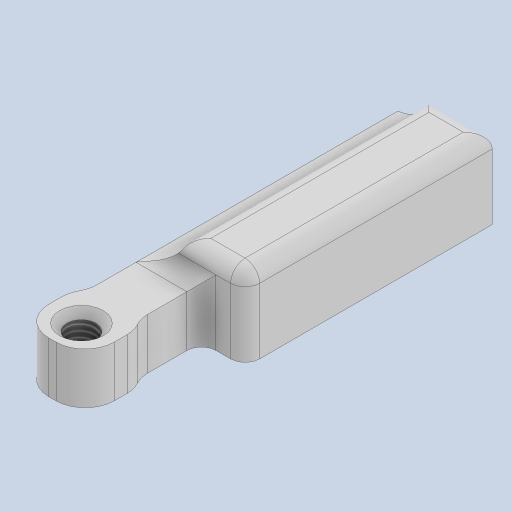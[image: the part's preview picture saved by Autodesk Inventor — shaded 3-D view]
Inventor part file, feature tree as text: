
AUTODESK INVENTOR PART (.ipt)
format: ipt  version: 2023 (Build 270158000, 158)  size: 300,544 bytes
history: native  units: mm
features: extrude x11, sketch x11, fillet x8, other x3, thread x3, chamfer x2
ambient origin geometry x8: Origin, YZ Plane, XZ Plane, XY Plane, X Axis, Y Axis, Z Axis, Center Point
bodies: Body1 (feature_tree)
feature tree (38):
  other  "Твердое тело1"
  extrude  "Выдавливание1"  Depth=3.5mm
  extrude  "Выдавливание2"  Depth=70.0mm
  extrude  "Выдавливание3"  Depth=3.5mm TaperAngle=0.0deg
  chamfer  "Фаска1"  Distance=3.0mm
  fillet  "Сопряжение3"  Radius=0.5mm
  fillet  "Сопряжение4"  Radius=3.5mm
  extrude  "Выдавливание4"  Depth=4.5mm
  chamfer  "Фаска2"  Distance=3.0mm
  extrude  "Выдавливание5"  Depth=0.5mm
  fillet  "Сопряжение5"  Radius=3.5mm
  fillet  "Сопряжение6"  Radius=3.5mm
  thread  "Резьба1"
  thread  "Резьба2"
  thread  "Резьба3"
  other  "РабПлоскость1"
  extrude  "Выдавливание8"  Depth=3.5mm
  extrude  "Выдавливание9"  Depth=3.0mm
  other  "РабПлоскость2"
  extrude  "Выдавливание11"  TaperAngle=0.0deg  [1 undecoded]
  extrude  "Выдавливание12"  Depth=2.0mm
  extrude  "Выдавливание13"  Depth=3.0mm
  extrude  "Выдавливание15"  Depth=2.0mm
  fillet  "Сопряжение18"  Radius=3.5mm
  fillet  "Сопряжение19"  Radius=0.5mm
  fillet  "Сопряжение20"  Radius=2.0mm
  fillet  "Сопряжение21"  Radius=2.0mm
  sketch  "Эскиз1"
  sketch  "Эскиз2"
  sketch  "Эскиз3"
  sketch  "Эскиз4"
  sketch  "Эскиз5"
  sketch  "Эскиз8"
  sketch  "Эскиз9"
  sketch  "Эскиз11"
  sketch  "Эскиз12"
  sketch  "Эскиз13"
  sketch  "Эскиз15"
note: 1 required parameter value undecoded (feature->parameter linkage not recoverable at this tier; creation-order binding heuristic only, values carry confidence <= 0.55)
